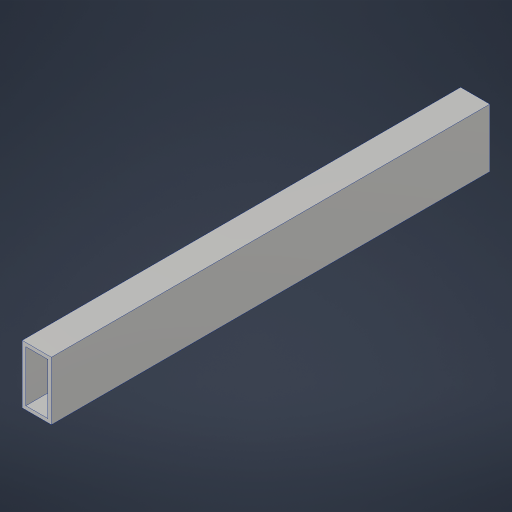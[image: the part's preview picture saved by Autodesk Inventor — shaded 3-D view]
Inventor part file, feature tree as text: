
AUTODESK INVENTOR PART (.ipt)
format: ipt  version: 2023.4 (Build 274418000, 418)  size: 167,424 bytes
history: native  units: in
note: dims shown in document units (in); Inventor stores cm internally (conversion verified against a paired STEP export)
features: extrude x1
ambient origin geometry x8: Origin, YZ Plane, XZ Plane, XY Plane, X Axis, Y Axis, Z Axis, Center Point
bodies: Solid1 (feature_tree)
feature tree (1):
  extrude  "Extrusion1"  TaperAngle=0.0deg  [1 undecoded]
note: 1 required parameter value undecoded (feature->parameter linkage not recoverable at this tier; creation-order binding heuristic only, values carry confidence <= 0.55)
